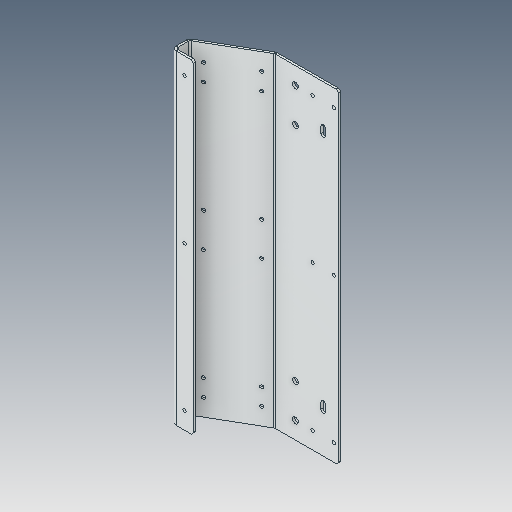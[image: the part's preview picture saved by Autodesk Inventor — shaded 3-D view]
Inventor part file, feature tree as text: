
AUTODESK INVENTOR PART (.ipt)
format: ipt  version: 2023.5 (Build 275446000, 446)  size: 146,432 bytes
history: native  units: in
note: dims shown in document units (in); Inventor stores cm internally (conversion verified against a paired STEP export)
features: fillet x1
ambient origin geometry x8: Origin, YZ Plane, XZ Plane, XY Plane, X Axis, Y Axis, Z Axis, Center Point
bodies: Solid1 (feature_tree)
feature tree (1):
  fillet  "Fillet1"  [1 undecoded]
note: 1 required parameter value undecoded (feature->parameter linkage not recoverable at this tier; creation-order binding heuristic only, values carry confidence <= 0.55)
